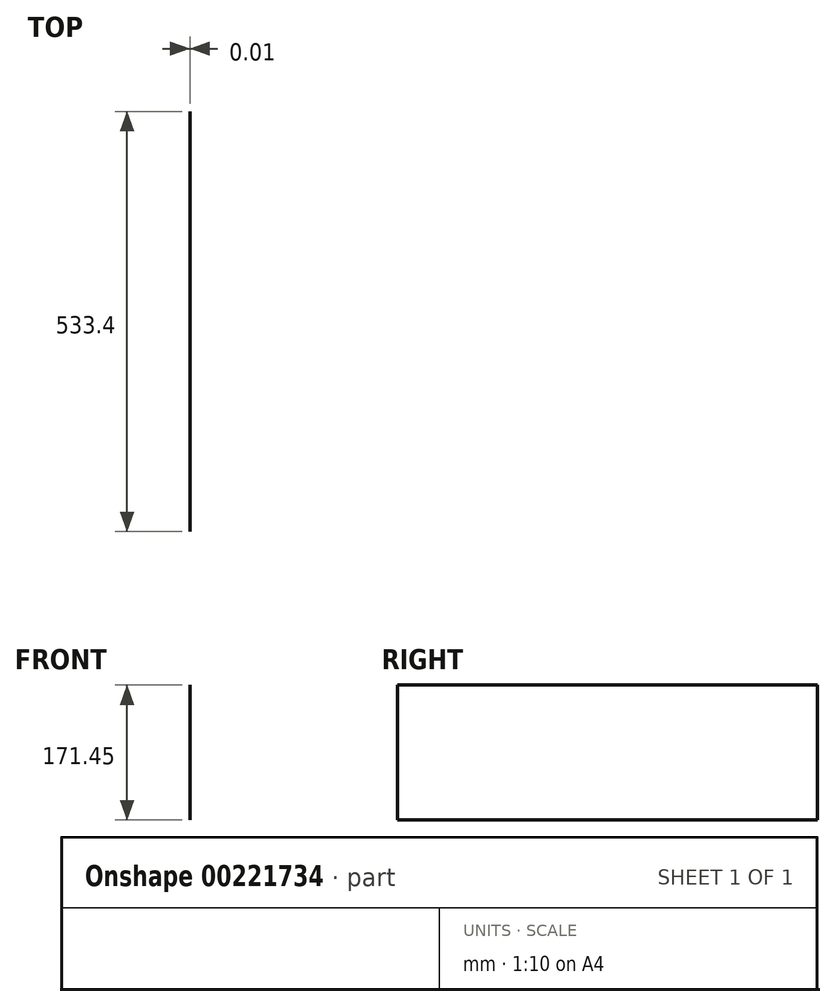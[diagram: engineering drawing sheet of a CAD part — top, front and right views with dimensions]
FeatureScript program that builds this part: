
annotation { "Feature Type Name" : "Feature", "Feature Type Description" : "" }
export const myFeature = defineFeature(function(context is Context, id is Id, definition is map)
    precondition{}
    {
        {
            var Q0;
            Q0=qCreatedBy(makeId("Right.planeOp"),FACE);
            var sketch = newSketch(context, id + "F0", { "sketchPlane" : qUnion([Q0])});
            skLineSegment(sketch, "E0.bottom", {"start": v(-368.23, -444.25) * mm, "end": v(165.17, -444.25) * mm});
            skLineSegment(sketch, "E0.top", {"start": v(-368.23, -272.8) * mm, "end": v(165.17, -272.8) * mm});
            skLineSegment(sketch, "E0.left", {"start": v(-368.23, -444.25) * mm, "end": v(-368.23, -272.8) * mm});
            skLineSegment(sketch, "E0.right", {"start": v(165.17, -444.25) * mm, "end": v(165.17, -272.8) * mm});
            skSolve(sketch);
        }
        {
            var Q0;
            Q0 = qSketchRegion(id + "F0", true);
            extrude(context, id + "F1", {"entities" : qUnion([Q0]), "oppositeDirection" : true, "depth" : 3 / 406.4 * mm});
        }
    });
